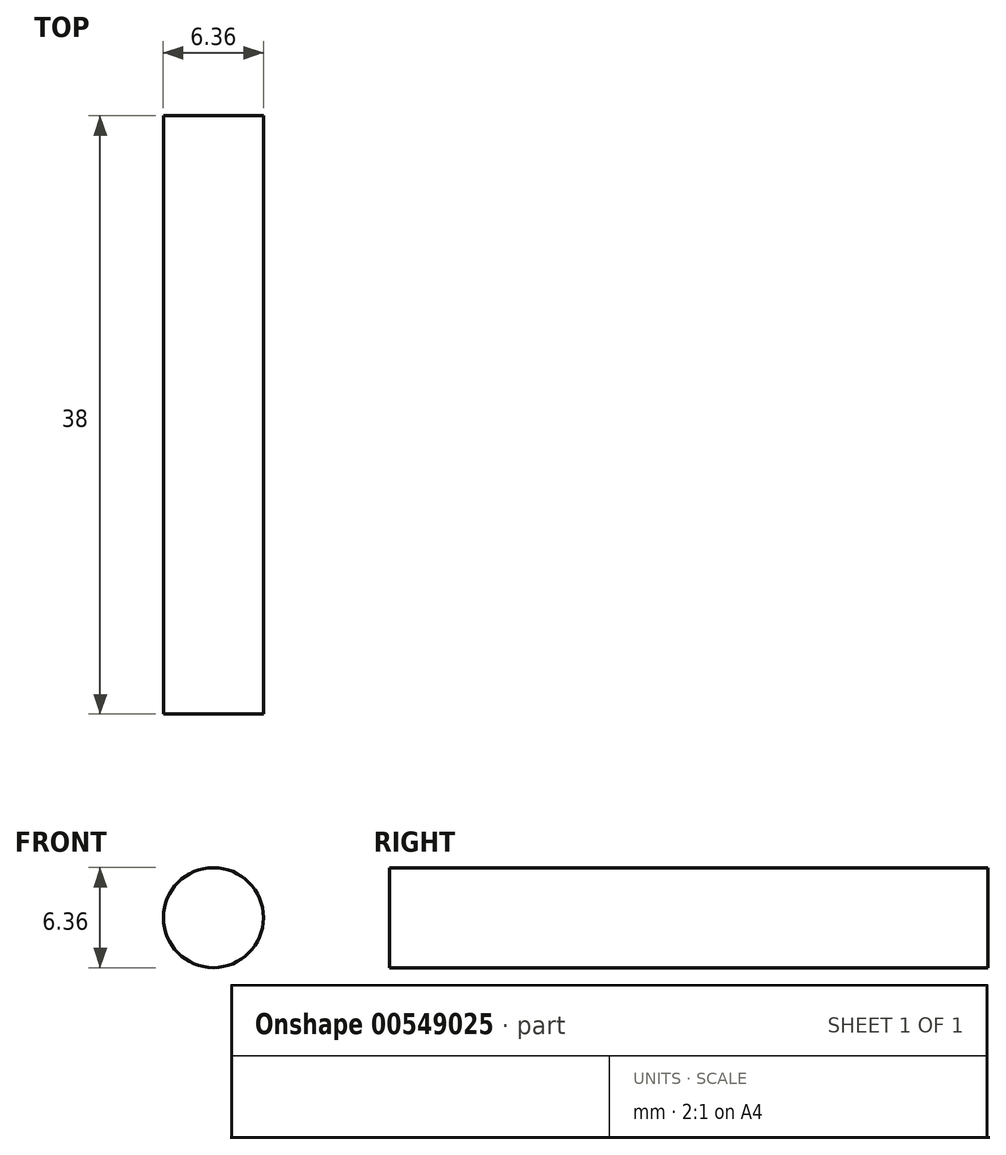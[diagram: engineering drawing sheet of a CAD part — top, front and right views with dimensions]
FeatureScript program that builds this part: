
annotation { "Feature Type Name" : "Feature", "Feature Type Description" : "" }
export const myFeature = defineFeature(function(context is Context, id is Id, definition is map)
    precondition{}
    {
        {
            var Q0;
            Q0=qCreatedBy(makeId("Front.planeOp"),FACE);
            var sketch = newSketch(context, id + "F0", { "sketchPlane" : qUnion([Q0])});
            skCircle(sketch, "E0", {"center": v(0, 0) * mm, "radius": 3.18 * mm});
            skSolve(sketch);
        }
        {
            var Q0;
            Q0 = qSketchRegion(id + "F0", true);
            extrude(context, id + "F1", {"entities" : qUnion([Q0]), "flatOperationType" : FlatOperationType.REMOVE, "depth" : 38 * mm, "offsetDistance" : 25 * mm, "domain" : OperationDomain.MODEL});
        }
    });
